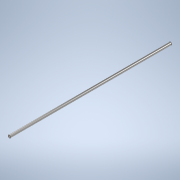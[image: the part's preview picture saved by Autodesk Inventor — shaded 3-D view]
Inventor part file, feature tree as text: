
AUTODESK INVENTOR PART (.ipt)
format: ipt  version: 2022 (Build 260153000, 153)  size: 96,256 bytes
history: native  units: mm
features: other x1, extrude x1, sketch x1
ambient origin geometry x8: Origin, YZ Plane, XZ Plane, XY Plane, X Axis, Y Axis, Z Axis, Center Point
bodies: Body1 (feature_tree)
feature tree (3):
  other  "Sólido1"
  extrude  "Extrusão1"  Depth=480.0mm TaperAngle=0.0deg
  sketch  "Esboço1"  dims[d0=8.0mm d1=480.0mm d2=0.0mm]
